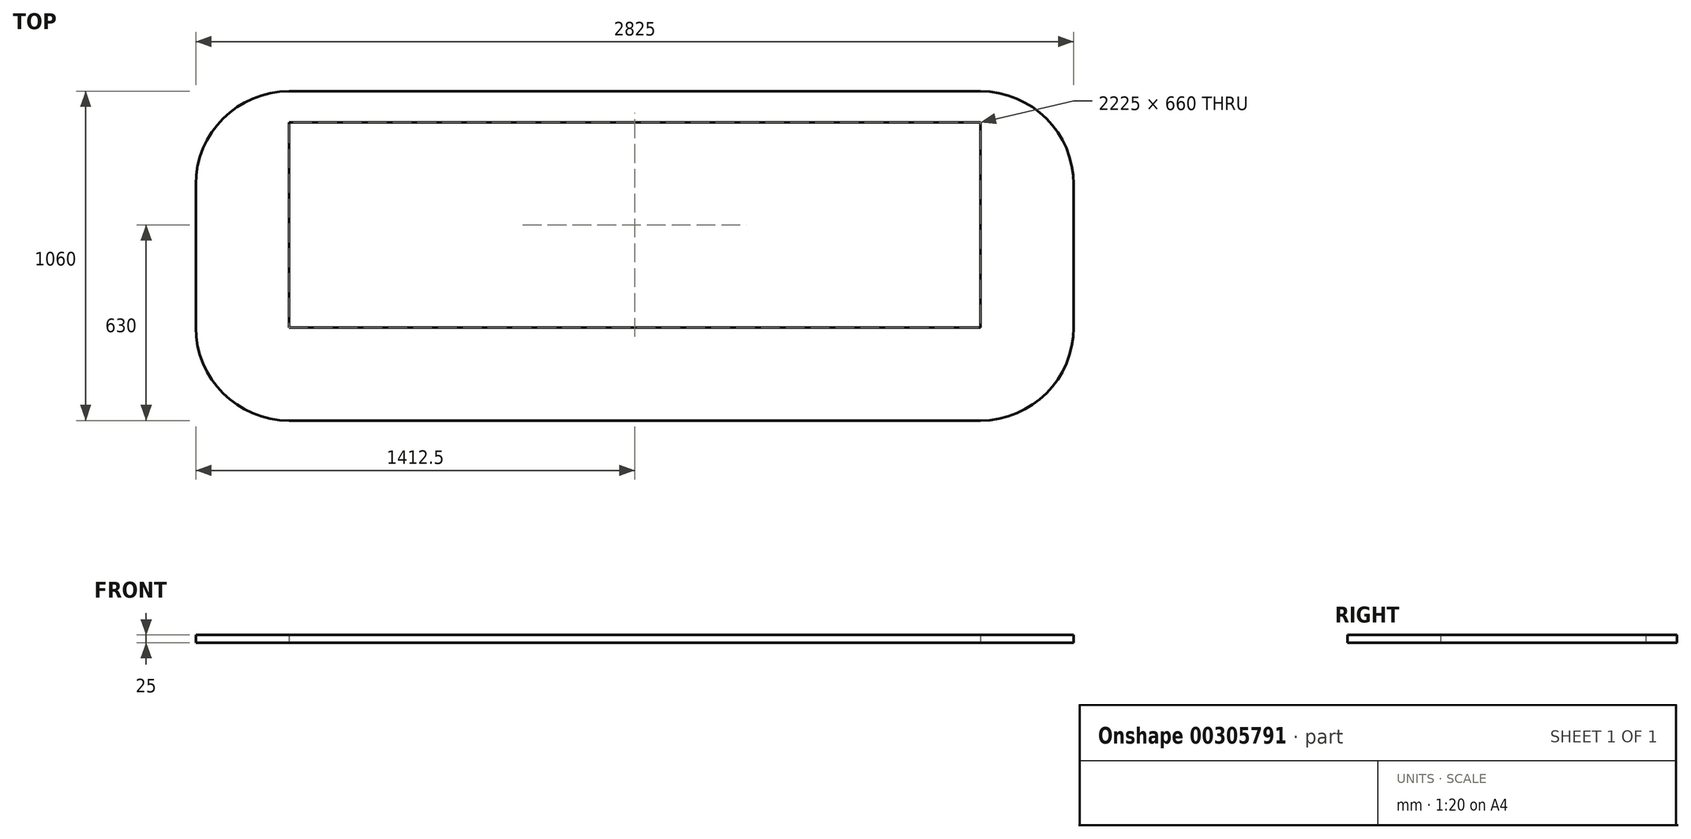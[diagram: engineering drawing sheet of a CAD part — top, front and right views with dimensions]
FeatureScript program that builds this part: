
annotation { "Feature Type Name" : "Feature", "Feature Type Description" : "" }
export const myFeature = defineFeature(function(context is Context, id is Id, definition is map)
    precondition{}
    {
        {
            var Q0;
            Q0=qCreatedBy(makeId("Top.planeOp"),FACE);
            var sketch = newSketch(context, id + "F0", { "sketchPlane" : qUnion([Q0])});
            skLineSegment(sketch, "E0.bottom", {"start": v(1112.5, 330) * mm, "end": v(-1112.5, 330) * mm});
            skLineSegment(sketch, "E0.top", {"start": v(1112.5, -330) * mm, "end": v(-1112.5, -330) * mm});
            skLineSegment(sketch, "E0.left", {"start": v(1112.5, 330) * mm, "end": v(1112.5, -330) * mm});
            skLineSegment(sketch, "E0.right", {"start": v(-1112.5, 330) * mm, "end": v(-1112.5, -330) * mm});
            skPoint(sketch, "E0.middle", {"position": v(0, 0) * mm});
            skLineSegment(sketch, "E1", {"start": v(-1112.5, 430) * mm, "end": v(1112.5, 430) * mm});
            skLineSegment(sketch, "E2", {"start": v(-1112.5, -630) * mm, "end": v(1112.5, -630) * mm});
            skLineSegment(sketch, "E3", {"start": v(-1412.5, 130) * mm, "end": v(-1412.5, -330) * mm});
            skPoint(sketch, "E4.orphan", {"position": v(-1212.5, 430) * mm});
            skPoint(sketch, "E5.orphan", {"position": v(-1212.5, -630) * mm});
            skPoint(sketch, "E6.visualSharp", {"position": v(-1412.5, 430) * mm});
            skArc(sketch, "E6.filletArc", {"start": v(-1112.5, 430) * mm, "mid": v(-1324.63, 342.13) * mm, "end": v(-1412.5, 130) * mm});
            skPoint(sketch, "E7.visualSharp", {"position": v(-1412.5, -630) * mm});
            skArc(sketch, "E7.filletArc", {"start": v(-1412.5, -330) * mm, "mid": v(-1324.63, -542.13) * mm, "end": v(-1112.5, -630) * mm});
            skLineSegment(sketch, "E8", {"start": v(1412.5, 130) * mm, "end": v(1412.5, -330) * mm});
            skPoint(sketch, "E9.visualSharp", {"position": v(1412.5, 430) * mm});
            skArc(sketch, "E9.filletArc", {"start": v(1412.5, 130) * mm, "mid": v(1324.63, 342.13) * mm, "end": v(1112.5, 430) * mm});
            skPoint(sketch, "E10.visualSharp", {"position": v(1412.5, -630) * mm});
            skArc(sketch, "E10.filletArc", {"start": v(1112.5, -630) * mm, "mid": v(1324.63, -542.13) * mm, "end": v(1412.5, -330) * mm});
            skSolve(sketch);
        }
        {
            var Q0;
            Q0 = qSketchRegion(id + "F0", true);
            extrude(context, id + "F1", {"entities" : qUnion([Q0]), "depth" : 25 * mm});
        }
    });
